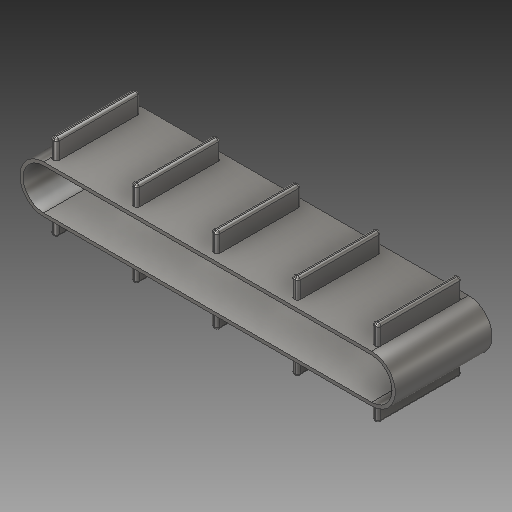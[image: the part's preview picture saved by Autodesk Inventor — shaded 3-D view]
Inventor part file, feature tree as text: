
AUTODESK INVENTOR PART (.ipt)
format: ipt  version: 2019 (Build 230136000, 136)  size: 408,576 bytes
history: native  units: mm
features: extrude x3, sketch x3, fillet x2
ambient origin geometry x8: Origin, YZ Plane, XZ Plane, XY Plane, X Axis, Y Axis, Z Axis, Center Point
bodies: Solid1 (feature_tree)
feature tree (8):
  extrude  "Extrusion1"  Depth=508.0mm
  extrude  "Extrusion2"  Depth=150.0mm TaperAngle=0.0deg
  fillet  "Fillet1"  Radius=10.0mm
  extrude  "Extrusion4"  Depth=10.0mm
  fillet  "Fillet3"  Radius=124.5mm
  sketch  "Sketch1"  dims[d0=63.5mm d1=508.0mm]
  sketch  "Sketch2"  dims[d2=73.5mm d3=150.0mm d4=0.0mm d5=10.0mm]
  sketch  "Sketch4"  dims[d6=20.0mm d8=140.0mm d9=10.0mm d11=10.0mm d13=10.0mm d14=50.0mm d16=124.5mm d17=10.0mm d19=10.0mm d21=30.0mm d22=0.0mm d23=4.0mm d43=10.0mm d44=20.0mm d46=140.0mm d47=10.0mm d49=10.0mm d51=10.0mm d52=50.0mm d54=124.5mm d55=10.0mm d57=10.0mm d59=30.0mm d60=0.0mm d61=4.0mm]
